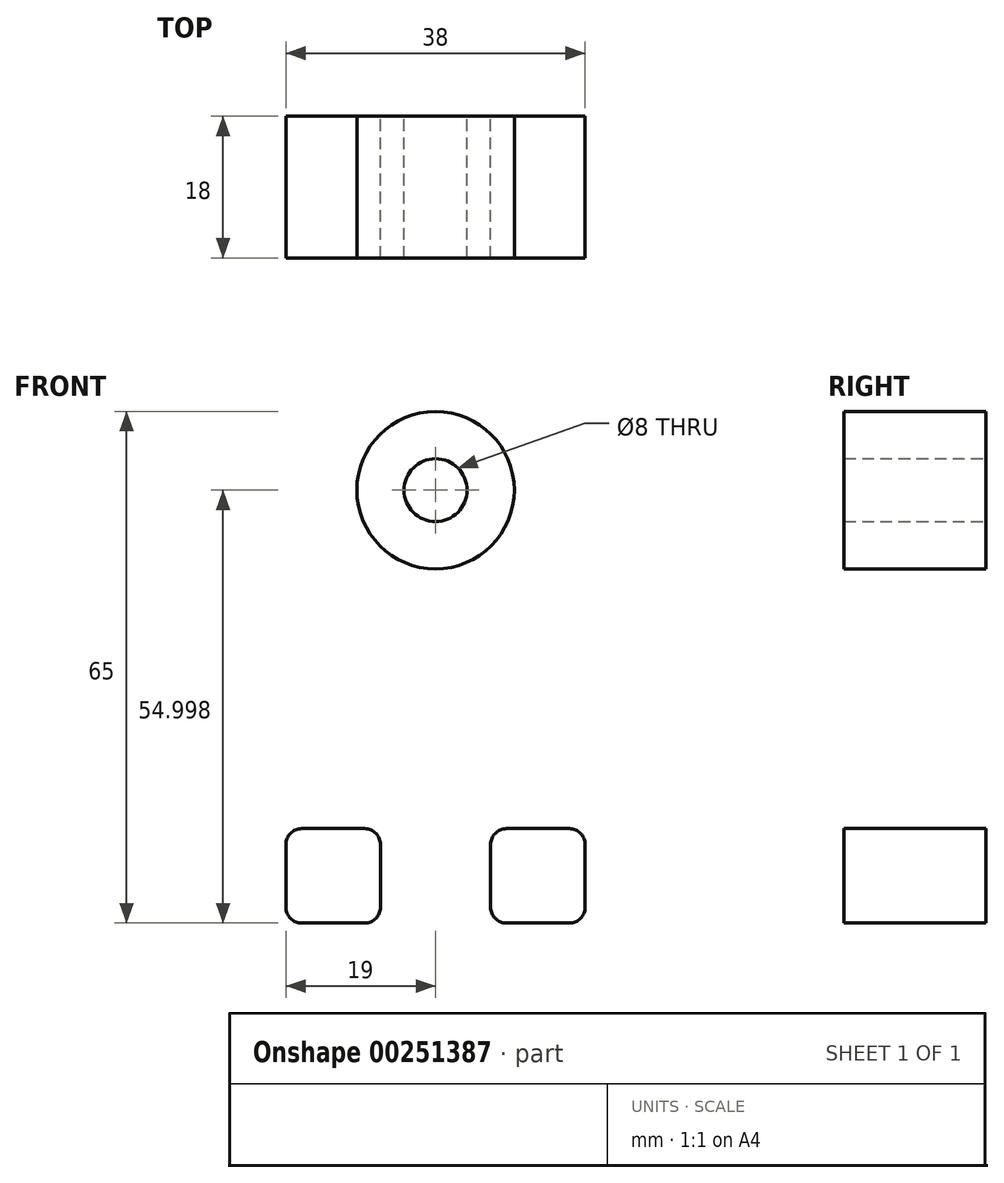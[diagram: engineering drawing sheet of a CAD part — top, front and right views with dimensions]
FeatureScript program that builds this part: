
annotation { "Feature Type Name" : "Feature", "Feature Type Description" : "" }
export const myFeature = defineFeature(function(context is Context, id is Id, definition is map)
    precondition{}
    {
        {
            var Q0;
            Q0=qCreatedBy(makeId("Front.planeOp"),FACE);
            var sketch = newSketch(context, id + "F0", { "sketchPlane" : qUnion([Q0])});
            skLineSegment(sketch, "E0", {"start": v(-17, -45.26) * mm, "end": v(17, -45.26) * mm});
            skLineSegment(sketch, "E1", {"start": v(-19, -43.26) * mm, "end": v(-19, -22.26) * mm});
            skLineSegment(sketch, "E2", {"start": v(-19, -22.26) * mm, "end": v(-19, -3.56) * mm});
            skCircle(sketch, "E3", {"center": v(0, 9.74) * mm, "radius": 10 * mm});
            skLineSegment(sketch, "E4", {"start": v(-19, -3.56) * mm, "end": v(-8.7, 14.66) * mm});
            skPoint(sketch, "E5.orphan", {"position": v(-19, 9.74) * mm});
            skLineSegment(sketch, "E6.MirrorCS", {"start": v(19, -22.26) * mm, "end": v(19, -3.56) * mm});
            skLineSegment(sketch, "E7.MirrorCS", {"start": v(19, -43.26) * mm, "end": v(19, -22.26) * mm});
            skLineSegment(sketch, "E8.MirrorCS", {"start": v(19, -3.56) * mm, "end": v(8.7, 14.66) * mm});
            skPoint(sketch, "E9.visualSharp", {"position": v(19, -45.26) * mm});
            skArc(sketch, "E9.filletArc", {"start": v(17, -45.26) * mm, "mid": v(18.41, -44.68) * mm, "end": v(19, -43.26) * mm});
            skPoint(sketch, "E10.visualSharp", {"position": v(-19, -45.26) * mm});
            skArc(sketch, "E10.filletArc", {"start": v(-19, -43.26) * mm, "mid": v(-18.41, -44.68) * mm, "end": v(-17, -45.26) * mm});
            skLineSegment(sketch, "E11", {"start": v(-7, -43.26) * mm, "end": v(-7, -35.26) * mm});
            skLineSegment(sketch, "E12", {"start": v(-9, -33.26) * mm, "end": v(-17, -33.26) * mm});
            skLineSegment(sketch, "E13", {"start": v(-19, -35.26) * mm, "end": v(-19, -43.26) * mm});
            skPoint(sketch, "E14.visualSharp", {"position": v(-19, -33.26) * mm});
            skArc(sketch, "E14.filletArc", {"start": v(-17, -33.26) * mm, "mid": v(-18.41, -33.85) * mm, "end": v(-19, -35.26) * mm});
            skPoint(sketch, "E15.visualSharp", {"position": v(-7, -33.26) * mm});
            skArc(sketch, "E15.filletArc", {"start": v(-7, -35.26) * mm, "mid": v(-7.59, -33.85) * mm, "end": v(-9, -33.26) * mm});
            skLineSegment(sketch, "E16", {"start": v(-9, -45.26) * mm, "end": v(-17, -45.26) * mm});
            skPoint(sketch, "E17.visualSharp", {"position": v(-7, -45.26) * mm});
            skArc(sketch, "E17.filletArc", {"start": v(-9, -45.26) * mm, "mid": v(-7.59, -44.68) * mm, "end": v(-7, -43.26) * mm});
            skLineSegment(sketch, "E18.MirrorCS", {"start": v(9, -33.26) * mm, "end": v(17, -33.26) * mm});
            skLineSegment(sketch, "E19.MirrorCS", {"start": v(7, -43.26) * mm, "end": v(7, -35.26) * mm});
            skArc(sketch, "E20.MirrorCS", {"start": v(7, -35.26) * mm, "mid": v(7.59, -33.85) * mm, "end": v(9, -33.26) * mm});
            skArc(sketch, "E21.MirrorCS", {"start": v(17, -33.26) * mm, "mid": v(18.41, -33.85) * mm, "end": v(19, -35.26) * mm});
            skArc(sketch, "E22.MirrorCS", {"start": v(9, -45.26) * mm, "mid": v(7.59, -44.68) * mm, "end": v(7, -43.26) * mm});
            skLineSegment(sketch, "E23", {"start": v(0, -45.26) * mm, "end": v(0, -22.26) * mm, "construction": true});
            skPoint(sketch, "E23.endSnap0", {"position": v(0, -45.26) * mm});
            skCircle(sketch, "E24", {"center": v(0, -22.26) * mm, "radius": 4 * mm});
            skCircle(sketch, "E25", {"center": v(0, 9.74) * mm, "radius": 4 * mm});
            skSolve(sketch);
        }
        {
            var Q0;
            Q0=makeQuery(id+"F0.imprint","IMPRINT",FACE,{"disambiguationData":[TD([[makeQuery(id+"F0.imprint","IMPRINT",EDGE,{"derivedFrom":sQuery(id+"F0.wireOp",EDGE,"E1")}),-1.0]])]});
            extrude(context, id + "F1", {"entities" : qUnion([Q0]), "depth" : 16 * mm});
        }
        {
            var Q0;
            Q0=makeQuery(id+"F0.imprint","IMPRINT",FACE,{"disambiguationData":[TD([[makeQuery(id+"F0.imprint","IMPRINT",EDGE,{"derivedFrom":sQuery(id+"F0.wireOp",EDGE,"E25")}),-1.0]])]});
            var Q1;
            Q1=makeQuery(id+"F0.imprint","IMPRINT",FACE,{"disambiguationData":[TD([[makeQuery(id+"F0.imprint","IMPRINT",EDGE,{"derivedFrom":sQuery(id+"F0.wireOp",EDGE,"E10.filletArc")}),1.0]])]});
            var Q2;
            {var subQ0=sQuery(id+"F0.wireOp",EDGE,"E9.filletArc");Q2=makeQuery(id+"F0.imprint","IMPRINT",FACE,{"disambiguationData":[TD([[makeQuery(id+"F0.imprint","IMPRINT",EDGE,{"derivedFrom":subQ0}),1.0]])]});}
            extrude(context, id + "F2", {"entities" : qUnion([Q0, Q1, Q2]), "operationType" : NewBodyOperationType.ADD, "depth" : 18 * mm});
        }
    });
